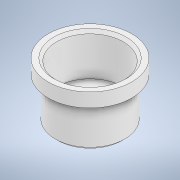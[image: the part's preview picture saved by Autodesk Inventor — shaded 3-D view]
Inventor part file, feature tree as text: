
AUTODESK INVENTOR PART (.ipt)
format: ipt  version: 2020 (Build 240168000, 168)  size: 147,456 bytes
history: native  units: mm
features: extrude x4, other x1, sketch x1, chamfer x1, fillet x1
ambient origin geometry x8: Origin, YZ Plane, XZ Plane, XY Plane, X Axis, Y Axis, Z Axis, Center Point
bodies: Body1 (feature_tree)
feature tree (8):
  other  "Bryła1"
  sketch  "Szkic1"
  extrude  "Wyciągnięcie proste1"  Depth=30.0mm
  extrude  "Wyciągnięcie proste2"  Depth=24.0mm
  extrude  "Wyciągnięcie proste3"  Depth=25.0mm
  chamfer  "Faza1"  Distance=20.0mm
  extrude  "Wyciągnięcie proste4"  Depth=15.0mm TaperAngle=0.0deg
  fillet  "Zaokrąglenie1"  Radius=15.0mm
